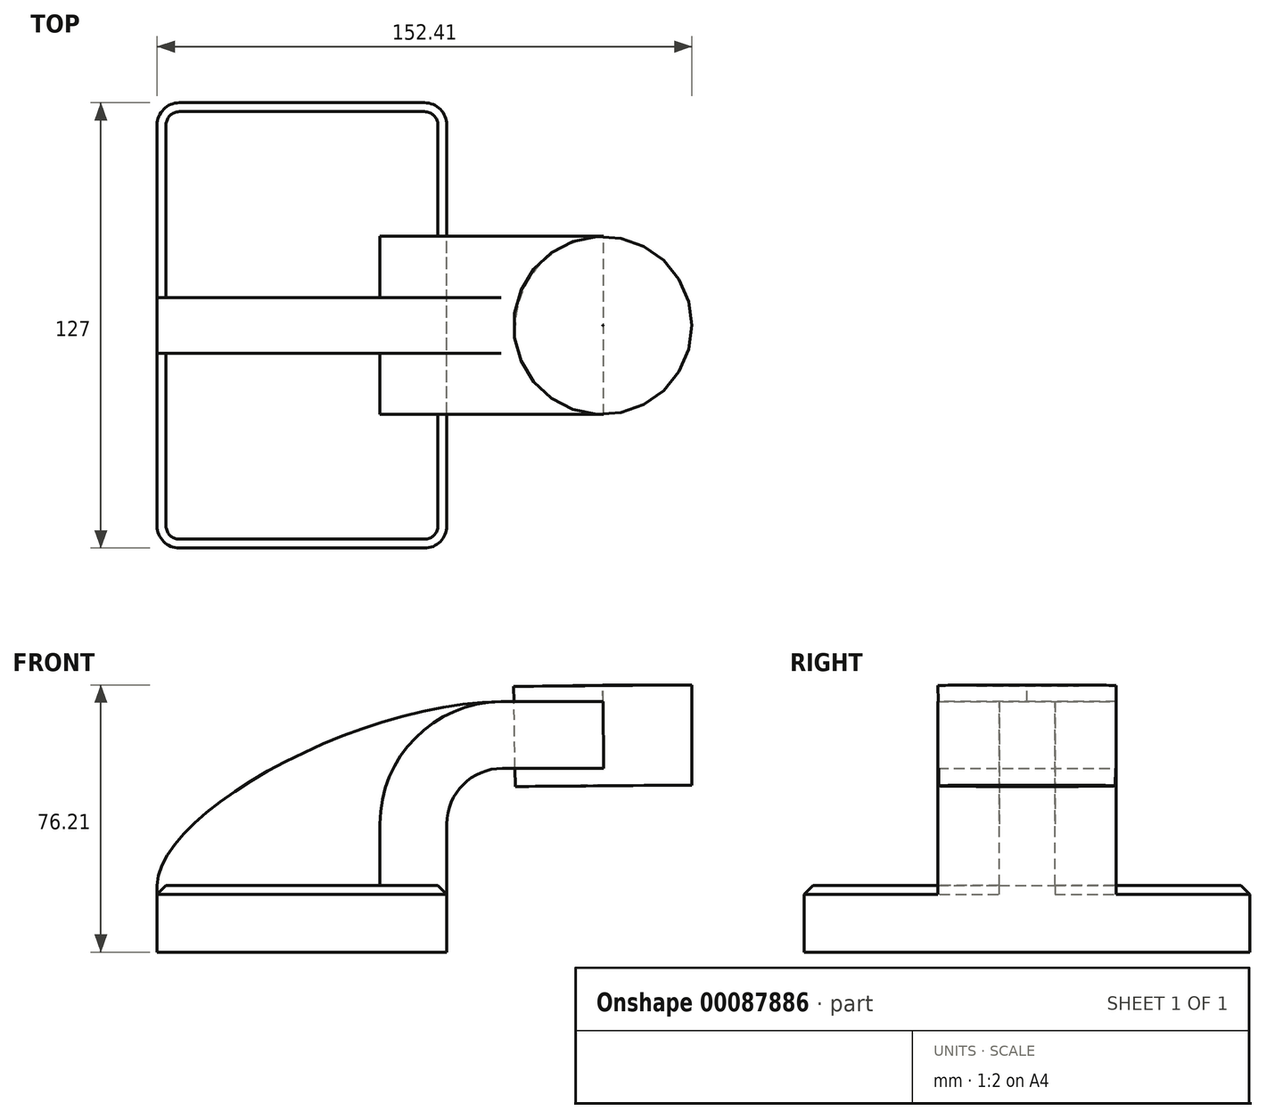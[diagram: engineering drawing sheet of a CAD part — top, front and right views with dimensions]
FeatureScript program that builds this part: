
annotation { "Feature Type Name" : "Feature", "Feature Type Description" : "" }
export const myFeature = defineFeature(function(context is Context, id is Id, definition is map)
    precondition{}
    {
        {
            var Q0;
            Q0=qCreatedBy(makeId("Front.planeOp"),FACE);
            var sketch = newSketch(context, id + "F0", { "sketchPlane" : qUnion([Q0])});
            skLineSegment(sketch, "E0.bottom", {"start": v(-41.28, 9.52) * mm, "end": v(41.28, 9.53) * mm});
            skLineSegment(sketch, "E0.top", {"start": v(-41.28, -9.53) * mm, "end": v(41.28, -9.53) * mm});
            skLineSegment(sketch, "E0.left", {"start": v(-41.28, 9.52) * mm, "end": v(-41.28, -9.53) * mm});
            skLineSegment(sketch, "E0.right", {"start": v(41.28, 9.53) * mm, "end": v(41.28, -9.52) * mm});
            skPoint(sketch, "E0.middle", {"position": v(0, 0) * mm});
            skLineSegment(sketch, "E1.bottom", {"start": v(60.32, 38.1) * mm, "end": v(111.12, 38.1) * mm});
            skLineSegment(sketch, "E1.top", {"start": v(60.32, 66.67) * mm, "end": v(111.12, 66.67) * mm});
            skLineSegment(sketch, "E1.left", {"start": v(60.32, 38.1) * mm, "end": v(60.32, 66.67) * mm});
            skLineSegment(sketch, "E1.right", {"start": v(111.12, 38.1) * mm, "end": v(111.12, 66.67) * mm});
            skPoint(sketch, "E1.middle", {"position": v(85.72, 52.39) * mm});
            skLineSegment(sketch, "E2", {"start": v(41.27, 9.53) * mm, "end": v(41.27, 27) * mm});
            skArc(sketch, "E3", {"start": v(41.27, 27) * mm, "mid": v(45.92, 38.23) * mm, "end": v(57.15, 42.88) * mm});
            skLineSegment(sketch, "E4", {"start": v(57.15, 42.88) * mm, "end": v(85.97, 42.88) * mm});
            skLineSegment(sketch, "E5.0", {"start": v(57.15, 61.93) * mm, "end": v(85.77, 61.93) * mm});
            skArc(sketch, "E5.1", {"start": v(22.22, 27) * mm, "mid": v(32.45, 51.7) * mm, "end": v(57.15, 61.93) * mm});
            skLineSegment(sketch, "E5.2", {"start": v(22.23, 9.53) * mm, "end": v(22.23, 27) * mm});
            skLineSegment(sketch, "E6", {"start": v(85.77, 61.93) * mm, "end": v(85.97, 38.1) * mm});
            skLineSegment(sketch, "E7", {"start": v(85.77, 61.93) * mm, "end": v(85.77, 66.67) * mm});
            skFitSpline(sketch, "E8", {"points": [v(-41.28, 9.53) * mm, v(57.15, 61.93) * mm], "startDerivative": vector(1.42, 62.9) * mm, "endDerivative": vector(121.42, 0.41) * mm});
            skSolve(sketch);
        }
        {
            var Q0;
            Q0=makeQuery(id+"F0.imprint","IMPRINT",FACE,{"disambiguationData":[TD([[makeQuery(id+"F0.imprint","IMPRINT",EDGE,{"derivedFrom":sQuery(id+"F0.wireOp",EDGE,"E0.top")}),1.0]])]});
            extrude(context, id + "F1", {"entities" : qUnion([Q0]), "endBound" : BoundingType.SYMMETRIC, "depth" : 127 * mm});
        }
        {
            var Q0;
            {var subQ1=sQuery(id+"F0.wireOp",EDGE,"E2");Q0=makeQuery(id+"F0.imprint","IMPRINT",FACE,{"disambiguationData":[TD([[makeQuery(id+"F0.imprint","IMPRINT",EDGE,{"derivedFrom":subQ1}),1.0]])]});}
            var Q1;
            {var subQ0=sQuery(id+"F0.wireOp",EDGE,"E4");var subQ1=sQuery(id+"F0.wireOp",EDGE,"E1.left");var subQ2=makeQuery(id+"F0.imprint","INTERSECT",VERTEX,{"derivedFrom":[subQ1,subQ0]});Q1=makeQuery(id+"F0.imprint","IMPRINT",FACE,{"disambiguationData":[TD([[makeQuery(id+"F0.imprint","IMPRINT",EDGE,{"disambiguationData":[TD([[subQ2,-1.0]])],"derivedFrom":subQ1}),-1.0]])]});}
            extrude(context, id + "F2", {"entities" : qUnion([Q0, Q1]), "operationType" : NewBodyOperationType.ADD, "endBound" : BoundingType.SYMMETRIC, "depth" : 50.8 * mm});
        }
        {
            var Q0;
            {var subQ3=sQuery(id+"F0.wireOp",EDGE,"E5.2");Q0=makeQuery(id+"F0.imprint","IMPRINT",FACE,{"disambiguationData":[TD([[makeQuery(id+"F0.imprint","IMPRINT",EDGE,{"derivedFrom":subQ3}),1.0]])]});}
            extrude(context, id + "F3", {"entities" : qUnion([Q0]), "operationType" : NewBodyOperationType.ADD, "endBound" : BoundingType.SYMMETRIC, "depth" : 15.88 * mm});
        }
        {
            var Q0;
            {var subQ0=sQuery(id+"F0.wireOp",EDGE,"E1.right");Q0=makeQuery(id+"F0.imprint","IMPRINT",FACE,{"disambiguationData":[TD([[makeQuery(id+"F0.imprint","IMPRINT",EDGE,{"derivedFrom":subQ0}),1.0]])]});}
            var Q1;
            Q1=sQuery(id+"F0.wireOp",EDGE,"E6");
            revolve(context, id + "F4", {"entities" : qUnion([Q0]), "axis" : qUnion([Q1]), "revolveType" : RevolveType.FULL});
        }
        {
            var Q0;
            Q0=makeQuery(id+"F1.opExtrude","CAP_EDGE",EDGE,{"disambiguationData":[OSD([sQuery(id+"F0.wireOp",EDGE,"E0.left")])],"isStart":true});
            var Q1;
            Q1=makeQuery(id+"F1.opExtrude","CAP_EDGE",EDGE,{"disambiguationData":[OSD([sQuery(id+"F0.wireOp",EDGE,"E0.left")])],"isStart":false});
            var Q2;
            Q2=makeQuery(id+"F1.opExtrude","CAP_EDGE",EDGE,{"disambiguationData":[OSD([sQuery(id+"F0.wireOp",EDGE,"E0.right")])],"isStart":false});
            var Q3;
            Q3=makeQuery(id+"F1.opExtrude","CAP_EDGE",EDGE,{"disambiguationData":[OSD([sQuery(id+"F0.wireOp",EDGE,"E0.right")])],"isStart":true});
            fillet(context, id + "F5", {"entities" : qUnion([Q0, Q1, Q2, Q3]), "radius" : 6.35 * mm, "tangentPropagation" : true, "allowEdgeOverflow" : false});
        }
        {
            var Q0;
            Q0=makeQuery(id+"F1.opExtrude","CAP_EDGE",EDGE,{"disambiguationData":[OSD([sQuery(id+"F0.wireOp",EDGE,"E0.bottom")])],"isStart":false});
            chamfer(context, id + "F6", {"entities" : qUnion([Q0]), "width" : 2.54 * mm, "tangentPropagation" : true});
        }
        {
            var Q0;
            Q0=makeQuery(id+"F1.opExtrude","CAP_EDGE",EDGE,{"disambiguationData":[OSD([sQuery(id+"F0.wireOp",EDGE,"E0.bottom")])],"isStart":true});
            chamfer(context, id + "F7", {"entities" : qUnion([Q0]), "width" : 2.54 * mm, "tangentPropagation" : true});
        }
    });
